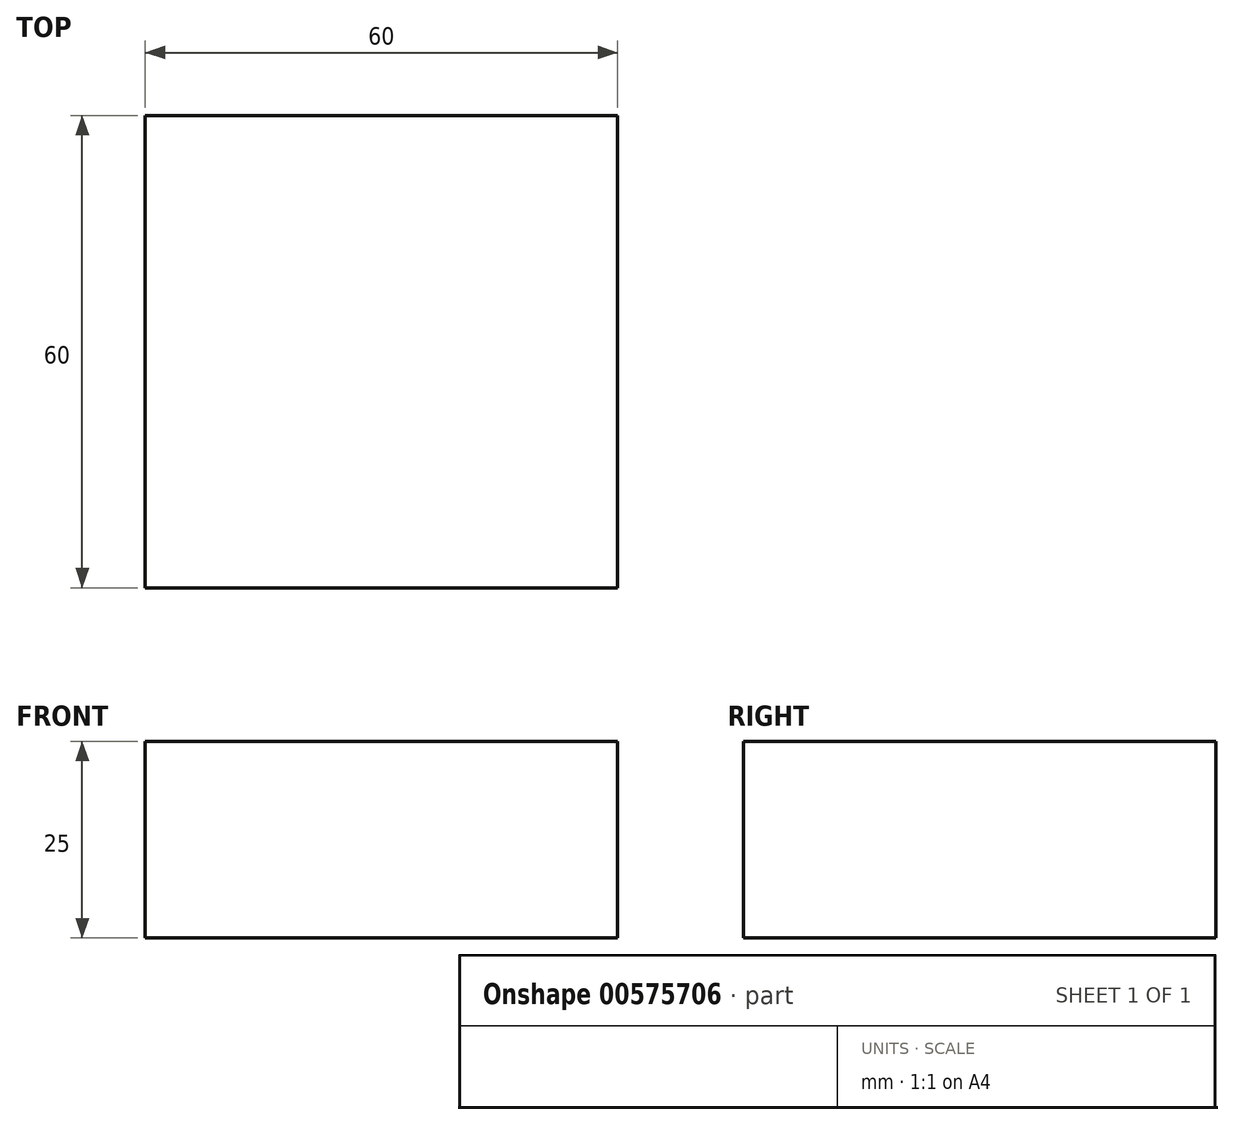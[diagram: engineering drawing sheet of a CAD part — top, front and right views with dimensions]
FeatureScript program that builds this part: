
annotation { "Feature Type Name" : "Feature", "Feature Type Description" : "" }
export const myFeature = defineFeature(function(context is Context, id is Id, definition is map)
    precondition{}
    {
        {
            var Q0;
            Q0=qCreatedBy(makeId("Top.planeOp"),FACE);
            var sketch = newSketch(context, id + "F0", { "sketchPlane" : qUnion([Q0])});
            skLineSegment(sketch, "E0.bottom", {"start": v(-30, 30) * mm, "end": v(30, 30) * mm});
            skLineSegment(sketch, "E0.top", {"start": v(-30, -30) * mm, "end": v(30, -30) * mm});
            skLineSegment(sketch, "E0.left", {"start": v(-30, 30) * mm, "end": v(-30, -30) * mm});
            skLineSegment(sketch, "E0.right", {"start": v(30, 30) * mm, "end": v(30, -30) * mm});
            skPoint(sketch, "E0.middle", {"position": v(0, 0) * mm});
            skSolve(sketch);
        }
        {
            var Q0;
            Q0 = qSketchRegion(id + "F0", true);
            extrude(context, id + "F1", {"entities" : qUnion([Q0]), "depth" : 25 * mm, "offsetDistance" : 25 * mm});
        }
    });
